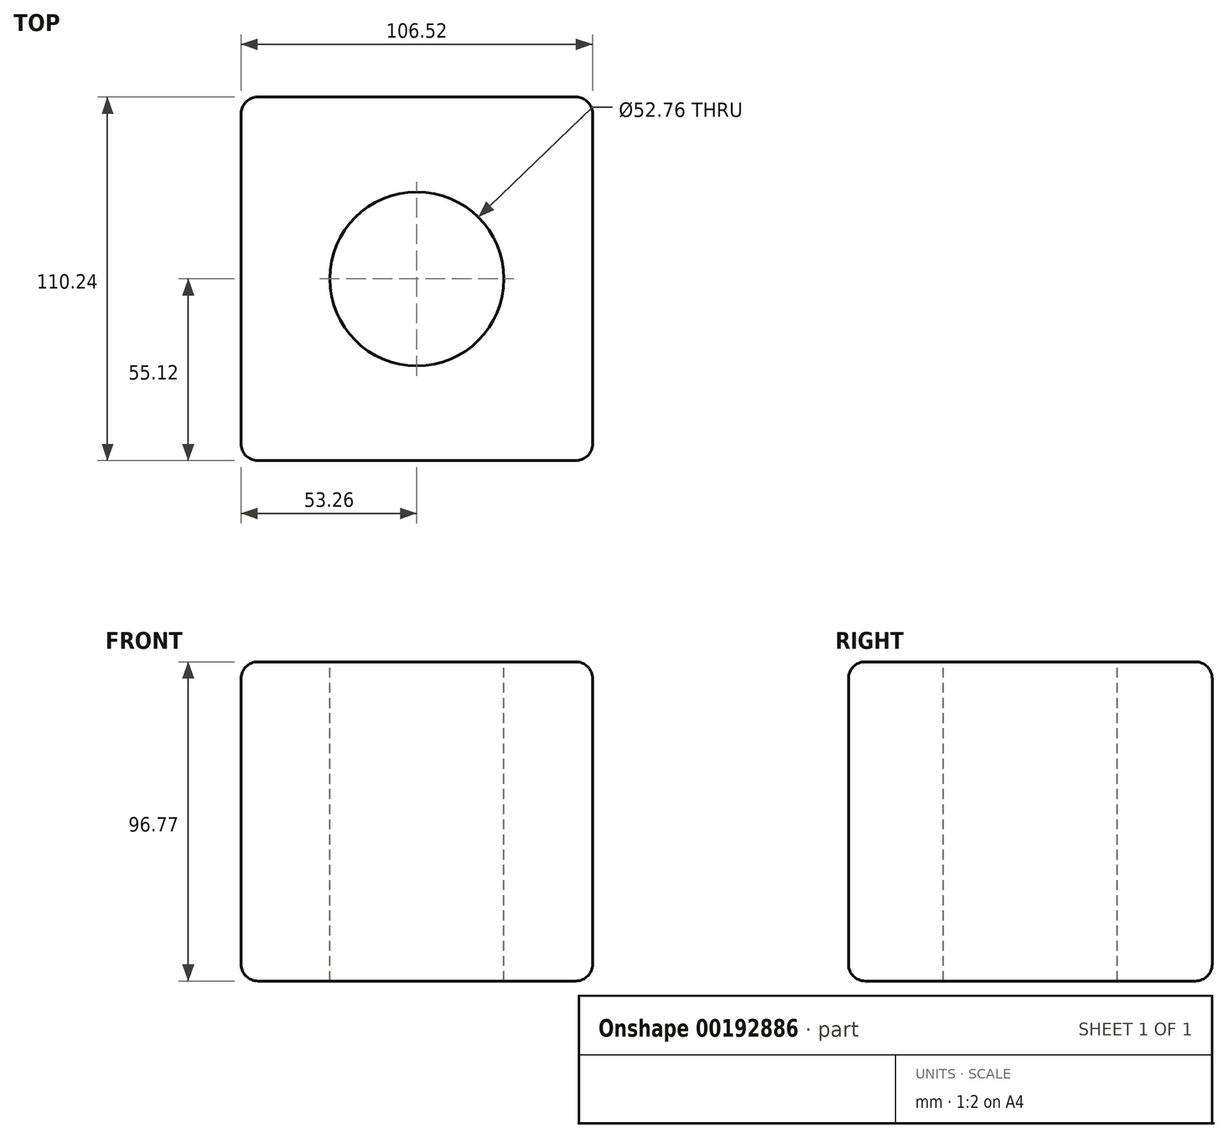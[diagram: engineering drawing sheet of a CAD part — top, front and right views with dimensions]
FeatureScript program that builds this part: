
annotation { "Feature Type Name" : "Feature", "Feature Type Description" : "" }
export const myFeature = defineFeature(function(context is Context, id is Id, definition is map)
    precondition{}
    {
        {
            var Q0;
            Q0=qCreatedBy(makeId("Top.planeOp"),FACE);
            var sketch = newSketch(context, id + "F0", { "sketchPlane" : qUnion([Q0])});
            skLineSegment(sketch, "E0.bottom", {"start": v(53.26, 55.12) * mm, "end": v(-53.26, 55.12) * mm});
            skLineSegment(sketch, "E0.top", {"start": v(53.26, -55.12) * mm, "end": v(-53.26, -55.12) * mm});
            skLineSegment(sketch, "E0.left", {"start": v(53.26, 55.12) * mm, "end": v(53.26, -55.12) * mm});
            skLineSegment(sketch, "E0.right", {"start": v(-53.26, 55.12) * mm, "end": v(-53.26, -55.12) * mm});
            skPoint(sketch, "E0.middle", {"position": v(0, 0) * mm});
            skSolve(sketch);
        }
        {
            var Q0;
            Q0 = qSketchRegion(id + "F0", true);
            extrude(context, id + "F1", {"entities" : qUnion([Q0]), "depth" : 96.77 * mm});
        }
        {
            var Q0;
            Q0=makeQuery(id+"F1.opExtrude","CAP_FACE",FACE,{"disambiguationData":[OSD([sQuery(id+"F0.wireOp",EDGE,"E0.bottom"),sQuery(id+"F0.wireOp",EDGE,"E0.top"),sQuery(id+"F0.wireOp",EDGE,"E0.left"),sQuery(id+"F0.wireOp",EDGE,"E0.right")])],"isStart":false});
            var sketch = newSketch(context, id + "F2", { "sketchPlane" : qUnion([Q0])});
            skCircle(sketch, "E1", {"center": v(0, 0) * mm, "radius": 26.38 * mm});
            skSolve(sketch);
        }
        {
            var Q0;
            Q0=makeQuery(id+"F2.imprint","IMPRINT",FACE,{"disambiguationData":[TD([[makeQuery(id+"F2.imprint","IMPRINT",EDGE,{"derivedFrom":sQuery(id+"F2.wireOp",EDGE,"E1")}),1.0]])]});
            extrude(context, id + "F3", {"entities" : qUnion([Q0]), "operationType" : NewBodyOperationType.REMOVE, "oppositeDirection" : true, "depth" : 130.8 * mm});
        }
        {
            var Q0;
            Q0=makeQuery(id+"F1.opExtrude","CAP_EDGE",EDGE,{"disambiguationData":[OSD([sQuery(id+"F0.wireOp",EDGE,"E0.bottom")])],"isStart":false});
            var Q1;
            Q1=makeQuery(id+"F1.opExtrude","CAP_EDGE",EDGE,{"disambiguationData":[OSD([sQuery(id+"F0.wireOp",EDGE,"E0.right")])],"isStart":false});
            var Q2;
            Q2=makeQuery(id+"F1.opExtrude","CAP_EDGE",EDGE,{"disambiguationData":[OSD([sQuery(id+"F0.wireOp",EDGE,"E0.top")])],"isStart":false});
            var Q3;
            Q3=makeQuery(id+"F1.opExtrude","CAP_EDGE",EDGE,{"disambiguationData":[OSD([sQuery(id+"F0.wireOp",EDGE,"E0.left")])],"isStart":false});
            var Q4;
            Q4=makeQuery(id+"F1.opExtrude","SWEPT_EDGE",EDGE,{"disambiguationData":[OSD([sQuery(id+"F0.wireOp",EDGE,"E0.top"),sQuery(id+"F0.wireOp",EDGE,"E0.left")])]});
            var Q5;
            Q5=makeQuery(id+"F1.opExtrude","SWEPT_EDGE",EDGE,{"disambiguationData":[OSD([sQuery(id+"F0.wireOp",EDGE,"E0.top"),sQuery(id+"F0.wireOp",EDGE,"E0.right")])]});
            var Q6;
            Q6=makeQuery(id+"F1.opExtrude","CAP_EDGE",EDGE,{"disambiguationData":[OSD([sQuery(id+"F0.wireOp",EDGE,"E0.top")])],"isStart":true});
            var Q7;
            Q7=makeQuery(id+"F1.opExtrude","CAP_EDGE",EDGE,{"disambiguationData":[OSD([sQuery(id+"F0.wireOp",EDGE,"E0.right")])],"isStart":true});
            var Q8;
            Q8=makeQuery(id+"F1.opExtrude","SWEPT_EDGE",EDGE,{"disambiguationData":[OSD([sQuery(id+"F0.wireOp",EDGE,"E0.bottom"),sQuery(id+"F0.wireOp",EDGE,"E0.right")])]});
            var Q9;
            Q9=makeQuery(id+"F1.opExtrude","CAP_EDGE",EDGE,{"disambiguationData":[OSD([sQuery(id+"F0.wireOp",EDGE,"E0.bottom")])],"isStart":true});
            var Q10;
            Q10=makeQuery(id+"F1.opExtrude","SWEPT_EDGE",EDGE,{"disambiguationData":[OSD([sQuery(id+"F0.wireOp",EDGE,"E0.bottom"),sQuery(id+"F0.wireOp",EDGE,"E0.left")])]});
            var Q11;
            Q11=makeQuery(id+"F1.opExtrude","CAP_EDGE",EDGE,{"disambiguationData":[OSD([sQuery(id+"F0.wireOp",EDGE,"E0.left")])],"isStart":true});
            fillet(context, id + "F4", {"entities" : qUnion([Q0, Q1, Q2, Q3, Q4, Q5, Q6, Q7, Q8, Q9, Q10, Q11]), "radius" : 5.08 * mm, "tangentPropagation" : true, "allowEdgeOverflow" : false});
        }
    });
